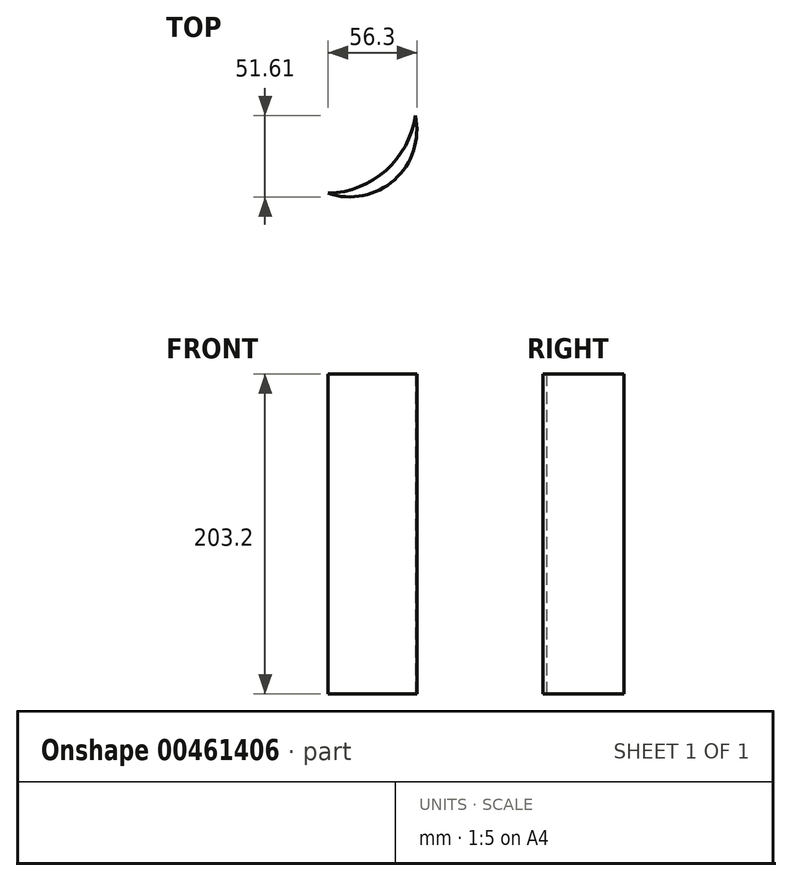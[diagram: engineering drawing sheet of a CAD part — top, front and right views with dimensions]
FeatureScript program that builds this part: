
annotation { "Feature Type Name" : "Feature", "Feature Type Description" : "" }
export const myFeature = defineFeature(function(context is Context, id is Id, definition is map)
    precondition{}
    {
        {
            var Q0;
            Q0=qCreatedBy(makeId("Top.planeOp"),FACE);
            var sketch = newSketch(context, id + "F0", { "sketchPlane" : qUnion([Q0])});
            skArc(sketch, "E0", {"start": v(-55.34, 0) * mm, "mid": v(-13.29, 8.53) * mm, "end": v(0, 49.34) * mm});
            skArc(sketch, "E1", {"start": v(-55.34, 0) * mm, "mid": v(-18.66, 14.56) * mm, "end": v(0, 49.34) * mm});
            skSolve(sketch);
        }
        {
            var Q0;
            Q0 = qSketchRegion(id + "F0", true);
            extrude(context, id + "F1", {"entities" : qUnion([Q0]), "endBound" : BoundingType.SYMMETRIC, "depth" : 203.2 * mm});
        }
    });
